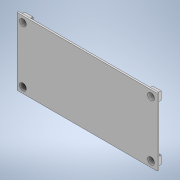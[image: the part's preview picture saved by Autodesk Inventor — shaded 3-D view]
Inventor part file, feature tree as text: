
AUTODESK INVENTOR PART (.ipt)
format: ipt  version: 2022 (Build 260153000, 153)  size: 146,432 bytes
history: native  units: mm
features: sketch x4, extrude x2, hole x2
ambient origin geometry x8: Origin, YZ Plane, XZ Plane, XY Plane, X Axis, Y Axis, Z Axis, Center Point
bodies: Volumenkörper1 (feature_tree)
feature tree (8):
  extrude  "Extrusion1"  Depth=166.0mm
  extrude  "Extrusion2"  Depth=2.2mm
  hole  "Bohrung1"  [1 undecoded]
  hole  "Bohrung2"  [1 undecoded]
  sketch  "Skizze1"  dims[d0=80.0mm d1=166.0mm]
  sketch  "Skizze2"  dims[d2=2.0mm d3=0.0mm d4=2.2mm]
  sketch  "Skizze3"  dims[d5=2.2mm d6=9.8mm]
  sketch  "Skizze4"  dims[d7=9.8mm d8=40.0mm d9=5.0mm d10=0.0mm d11=7.0mm d12=7.0mm d13=3.5mm d14=6.0mm d15=4.0mm d16=2.0mm d17=90.0deg d18=8.0mm d19=20.594885mm d20=8.0mm d21=6.0mm d22=4.0mm d23=2.0mm d24=90.0deg d25=5.0mm d26=20.594885mm]
note: 2 required parameter values undecoded (feature->parameter linkage not recoverable at this tier; creation-order binding heuristic only, values carry confidence <= 0.55)
